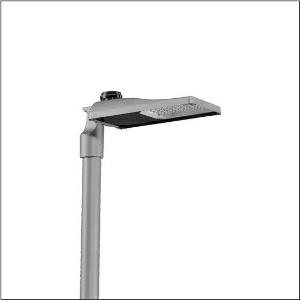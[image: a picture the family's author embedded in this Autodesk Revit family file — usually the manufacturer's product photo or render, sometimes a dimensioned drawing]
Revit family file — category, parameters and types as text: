
# Revit family: streetlight_sl_31_mini___st1_0a_5xh6d3bn08ha_24b0
name_source: partatom
category: Lighting Fixtures
units: mm (PartAtom-declared; Revit-internal decimal feet)

## family parameters
Cut with Voids When Loaded = No
Host = Face
Light Source = No
Part Type = Normal
Room Calculation Point = No
Round Connector Dimension = Use Diameter
Shared = No

## types (1)
- --- (1 x LED, 9240 lm, 68.3 W, 3000K)
    Apparent Load = 68 VA
    CIE Flux Codes = 37 72 97 100 100
    Color Rendering = 70
    Color Temperature = 3000K
    Default Elevation = 1800 mm
    Description = Streetlight SL 31 mini NEMA (7pin) mast luminaire for post-top, side-entry; light control with lens of PMMA; light distribution: ST1.0a, direct asymmetric distribution, for standard-compliant lighting for roads and squares; LED: luminous flux: 9.240lm, light colour: 730, colour temperature: 3000K; luminous efficacy: 135,3lm/W; control: pre-setting: linear dimming characteristic, flexible luminous flux parameterisation, time-dependent luminous flux control, constant luminous flux control, intelligent temperature release in ECG and LED module, overheat protection; luminaire housing, of diecast aluminium, SITECO metallic grey (DB 702S), corrosivity category C5 high according to DIN EN ISO 12944; cover of toughened safety glass, transparent, opened without tools; mast flange of diecast aluminium, SITECO metallic grey (DB 702S), spigot size: 76/60mm, mast flange included unmounted; cable length: 8,5m, connection cable pre-assembled; mains connection: 220..240V, AC, 50/60Hz; power consumption (at start of service life): 68,3W / (at end of service life): 74,8W / (with reduced operation 50%): 29,7W; protection rating (complete): IP66; insulation class (complete): insulation class I (protective earthing); impact resistance: IK10; certification: CE, ENEC, ENEC+, VDE, UKCA; permissible operating ambient temperature for outdoor applications: -40..+50°C; packaging unit: 1 piece

Light Distribution: ST1.0a
    Height = 76 mm
    Lamp = 1 x LED
    Lamp Light Flux = 9240 lm
    Lamp Power = 68.3 W
    Lamp count = 1
    Length = 547 mm
    Luminous efficacy = 135 lm/W
    Manufacturer = Siteco
    ModVariant = No
    Model = 5XH6D3BN08HA
    Number of Poles = 1
    OnlyDefault = Yes
    Power Factor = 1
    Product Name = Streetlight SL 31 mini | ST1.0a
    Product group = mast luminaire | pylon top
    ProductGroupID = 6100
    Protection Class = Protection class I
    Protection Degree = IP 66
    RLX_Detail_Level = 1
    RLX_Emergency_Light_Flux = 0 lm
    RLX_Emergency_Type = 0
    RLX_Emergency_Type_DB = No
    RlxData = <blob elided: 39953 chars, md5=2708e6be>
    Socket = socket
    Standby Power = 0 W
    System Light Flux = 9240 lm
    System Power = 68 W
    Type Comments = factory setting: luminous flux: 100 % | dim-lin: 254 | 693 mA
    Type Image = l_1300322.jpg
    URL = http://relux.com
    VarID = @adj_060429
    Voltage = 0 V
    Weight = 0.00 kg
    Width = 265 mm

## geometry (parser evidence)
native form markers: Blend x4, Sweep x9
no freeform markers — native parametric forms only
